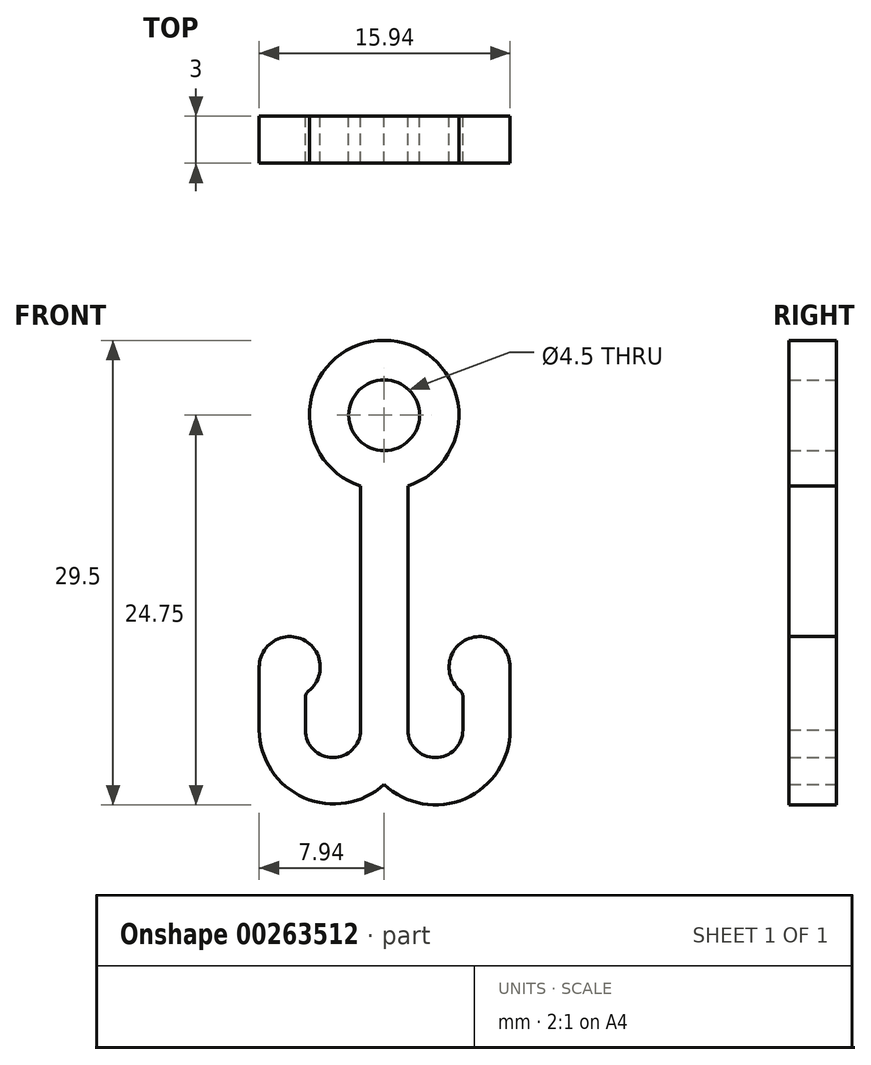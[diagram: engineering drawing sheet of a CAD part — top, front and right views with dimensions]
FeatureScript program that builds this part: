
annotation { "Feature Type Name" : "Feature", "Feature Type Description" : "" }
export const myFeature = defineFeature(function(context is Context, id is Id, definition is map)
    precondition{}
    {
        {
            var Q0;
            Q0=qCreatedBy(makeId("Front.planeOp"),FACE);
            var sketch = newSketch(context, id + "F1", { "sketchPlane" : qUnion([Q0])});
            skCircle(sketch, "E0", {"center": v(0, 0) * mm, "radius": 2.25 * mm});
            skArc(sketch, "E1", {"start": v(1.5, -4.5) * mm, "mid": v(0, 4.75) * mm, "end": v(-1.5, -4.5) * mm});
            skLineSegment(sketch, "E2", {"start": v(1.5, -4.5) * mm, "end": v(1.5, -20) * mm});
            skArc(sketch, "E3", {"start": v(-5, -20) * mm, "mid": v(-3.25, -21.75) * mm, "end": v(-1.5, -20) * mm});
            skArc(sketch, "E4", {"start": v(1.5, -20) * mm, "mid": v(3.25, -21.75) * mm, "end": v(5, -20) * mm});
            skArc(sketch, "E5", {"start": v(0, -23.46) * mm, "mid": v(5.14, -24.36) * mm, "end": v(8, -20) * mm});
            skPoint(sketch, "E6.end.orphan", {"position": v(-5, -20) * mm});
            skPoint(sketch, "E7.end.orphan", {"position": v(5, -20) * mm});
            skPoint(sketch, "E8.startSnap0", {"position": v(-6.03, -20) * mm});
            skLineSegment(sketch, "E9", {"start": v(-7.94, -20) * mm, "end": v(-7.94, -16) * mm});
            skLineSegment(sketch, "E10", {"start": v(8, -20) * mm, "end": v(8, -16) * mm});
            skArc(sketch, "E11", {"start": v(-4.8, -17.53) * mm, "mid": v(-5.15, -14.26) * mm, "end": v(-7.94, -16) * mm});
            skArc(sketch, "E12", {"start": v(8, -16) * mm, "mid": v(5.24, -14.24) * mm, "end": v(4.82, -17.49) * mm});
            skPoint(sketch, "E13.orphan", {"position": v(-6.03, -9.04) * mm});
            skArc(sketch, "E14.trimOffspring", {"start": v(-7.94, -20) * mm, "mid": v(-5.09, -24.3) * mm, "end": v(0, -23.46) * mm});
            skLineSegment(sketch, "E15", {"start": v(-5, -20) * mm, "end": v(-5, -17.92) * mm});
            skLineSegment(sketch, "E16", {"start": v(5, -20) * mm, "end": v(5, -17.87) * mm});
            skPoint(sketch, "E17.start.orphan", {"position": v(-4.12, -20) * mm});
            skPoint(sketch, "E18.orphan", {"position": v(4.12, -20) * mm});
            skPoint(sketch, "E19.orphan", {"position": v(5.62, -20) * mm});
            skLineSegment(sketch, "E20.trimOffspring", {"start": v(-1.5, -4.5) * mm, "end": v(-1.5, -20) * mm});
            skPoint(sketch, "E21.start.orphan", {"position": v(-1.5, 0) * mm});
            skPoint(sketch, "E22.orphan", {"position": v(1.5, 0) * mm});
            skPoint(sketch, "E23.visualSharp", {"position": v(-5, -17.66) * mm});
            skArc(sketch, "E23.filletArc", {"start": v(-4.8, -17.53) * mm, "mid": v(-4.95, -17.7) * mm, "end": v(-5, -17.92) * mm});
            skPoint(sketch, "E24.visualSharp", {"position": v(5, -17.62) * mm});
            skArc(sketch, "E24.filletArc", {"start": v(5, -17.87) * mm, "mid": v(4.95, -17.66) * mm, "end": v(4.82, -17.49) * mm});
            skSolve(sketch);
        }
        {
            var Q0;
            Q0 = qSketchRegion(id + "F1", true);
            extrude(context, id + "F0", {"entities" : qUnion([Q0]), "depth" : 3 * mm});
        }
    });
